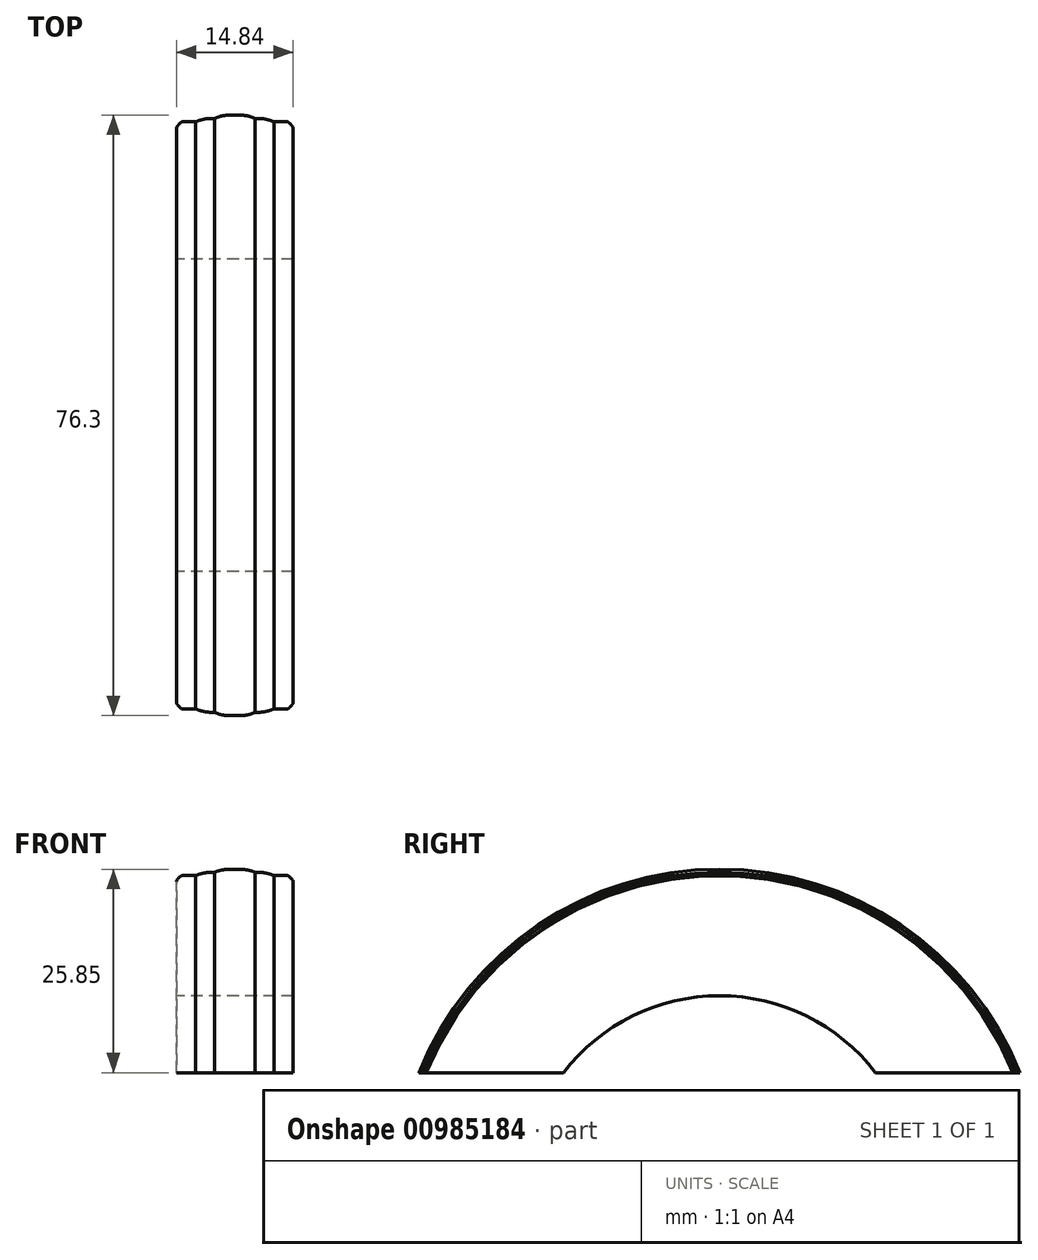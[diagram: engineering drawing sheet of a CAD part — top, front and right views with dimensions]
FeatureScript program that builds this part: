
annotation { "Feature Type Name" : "Feature", "Feature Type Description" : "" }
export const myFeature = defineFeature(function(context is Context, id is Id, definition is map)
    precondition{}
    {
        {
            var Q0;
            Q0=qCreatedBy(makeId("Front.planeOp"),FACE);
            var sketch = newSketch(context, id + "F0", { "sketchPlane" : qUnion([Q0])});
            skLineSegment(sketch, "E0", {"start": v(-55.67, 0) * mm, "end": v(68.03, 0) * mm, "construction": true});
            skLineSegment(sketch, "E1", {"start": v(-7.42, 0) * mm, "end": v(-7.42, 40.28) * mm});
            skLineSegment(sketch, "E2", {"start": v(-7.42, 40.28) * mm, "end": v(-4.96, 40.28) * mm});
            skLineSegment(sketch, "E3", {"start": v(-4.96, 40.28) * mm, "end": v(-4.96, 40.68) * mm});
            skLineSegment(sketch, "E4", {"start": v(-4.96, 40.68) * mm, "end": v(-2.58, 40.68) * mm});
            skLineSegment(sketch, "E5", {"start": v(-2.58, 40.68) * mm, "end": v(-2.58, 41.08) * mm});
            skLineSegment(sketch, "E6", {"start": v(-2.58, 41.08) * mm, "end": v(2.58, 41.08) * mm});
            skLineSegment(sketch, "E7", {"start": v(2.58, 41.08) * mm, "end": v(2.58, 40.68) * mm});
            skLineSegment(sketch, "E8", {"start": v(2.58, 40.68) * mm, "end": v(4.96, 40.68) * mm});
            skLineSegment(sketch, "E9", {"start": v(4.96, 40.68) * mm, "end": v(4.96, 40.28) * mm});
            skLineSegment(sketch, "E10", {"start": v(4.96, 40.28) * mm, "end": v(7.42, 40.28) * mm});
            skLineSegment(sketch, "E11", {"start": v(7.42, 40.28) * mm, "end": v(7.42, 0) * mm});
            skLineSegment(sketch, "E12", {"start": v(7.42, 0) * mm, "end": v(-7.42, 0) * mm});
            skLineSegment(sketch, "E13", {"start": v(0, 0) * mm, "end": v(0, 47.43) * mm, "construction": true});
            skSolve(sketch);
        }
        {
            var Q0;
            Q0=makeQuery(id+"F0.imprint","IMPRINT",FACE,{"disambiguationData":[TD([[makeQuery(id+"F0.imprint","IMPRINT",EDGE,{"derivedFrom":sQuery(id+"F0.wireOp",EDGE,"E1")}),-1.0]])]});
            var Q1;
            Q1=sQuery(id+"F0.wireOp",EDGE,"E0");
            revolve(context, id + "F1", {"surfaceOperationType" : NewSurfaceOperationType.NEW, "entities" : qUnion([Q0]), "axis" : qUnion([Q1]), "revolveType" : RevolveType.FULL});
        }
        {
            var Q0;
            Q0=makeQuery(id+"F1.opRevolve","SWEPT_EDGE",EDGE,{"disambiguationData":[OSD([sQuery(id+"F0.wireOp",EDGE,"E10"),sQuery(id+"F0.wireOp",EDGE,"E11")])]});
            var Q1;
            Q1=makeQuery(id+"F1.opRevolve","SWEPT_EDGE",EDGE,{"disambiguationData":[OSD([sQuery(id+"F0.wireOp",EDGE,"E1"),sQuery(id+"F0.wireOp",EDGE,"E2")])]});
            fillet(context, id + "F2", {"entities" : qUnion([Q0, Q1]), "radius" : 0.76 * mm, "tangentPropagation" : true, "rho" : 0.2, "crossSection" : FilletCrossSection.CONIC, "allowEdgeOverflow" : false});
        }
        {
            var Q0;
            Q0=makeQuery(id+"F1.opRevolve","SWEPT_EDGE",EDGE,{"disambiguationData":[OSD([sQuery(id+"F0.wireOp",EDGE,"E8"),sQuery(id+"F0.wireOp",EDGE,"E9")])]});
            var Q1;
            Q1=makeQuery(id+"F1.opRevolve","SWEPT_EDGE",EDGE,{"disambiguationData":[OSD([sQuery(id+"F0.wireOp",EDGE,"E3"),sQuery(id+"F0.wireOp",EDGE,"E4")])]});
            fillet(context, id + "F3", {"entities" : qUnion([Q0, Q1]), "radius" : 5.08 * mm, "tangentPropagation" : true, "allowEdgeOverflow" : false});
        }
        {
            var Q0;
            Q0=makeQuery(id+"F1.opRevolve","SWEPT_EDGE",EDGE,{"disambiguationData":[OSD([sQuery(id+"F0.wireOp",EDGE,"E6"),sQuery(id+"F0.wireOp",EDGE,"E7")])]});
            var Q1;
            Q1=makeQuery(id+"F1.opRevolve","SWEPT_EDGE",EDGE,{"disambiguationData":[OSD([sQuery(id+"F0.wireOp",EDGE,"E5"),sQuery(id+"F0.wireOp",EDGE,"E6")])]});
            fillet(context, id + "F4", {"entities" : qUnion([Q0, Q1]), "radius" : 5.08 * mm, "tangentPropagation" : true, "allowEdgeOverflow" : false});
        }
        {
            var Q0;
            Q0=qCreatedBy(makeId("Right.planeOp"),FACE);
            var sketch = newSketch(context, id + "F5", { "sketchPlane" : qUnion([Q0])});
            skCircle(sketch, "E14", {"center": v(0, 0) * mm, "radius": 25 * mm});
            skSolve(sketch);
        }
        {
            var Q0;
            Q0=qSketchRegion(id+"F5",true);
            extrude(context, id + "F6", {"entities" : qUnion([Q0]), "operationType" : NewBodyOperationType.REMOVE, "endBound" : BoundingType.THROUGH_ALL, "depth" : 25.4 * mm, "offsetDistance" : 25.4 * mm, "hasSecondDirection" : true, "secondDirectionBound" : SecondDirectionBoundingType.THROUGH_ALL, "secondDirectionOppositeDirection" : true, "secondDirectionDepth" : 25.4 * mm});
        }
        {
            var Q0;
            Q0=qCreatedBy(makeId("Right.planeOp"),FACE);
            var sketch = newSketch(context, id + "F7", { "sketchPlane" : qUnion([Q0])});
            skLineSegment(sketch, "E15", {"start": v(0, 15.23) * mm, "end": v(-38.1, 15.23) * mm, "construction": true});
            skLineSegment(sketch, "E16.MirrorCS", {"start": v(0, 15.23) * mm, "end": v(38.1, 15.23) * mm, "construction": true});
            skLineSegment(sketch, "E17", {"start": v(-59.25, 15.23) * mm, "end": v(65.7, 15.23) * mm});
            skLineSegment(sketch, "E18", {"start": v(65.7, 15.23) * mm, "end": v(65.7, -43.9) * mm});
            skLineSegment(sketch, "E19", {"start": v(65.7, -43.9) * mm, "end": v(-59.25, -43.9) * mm});
            skLineSegment(sketch, "E20", {"start": v(-59.25, -43.9) * mm, "end": v(-59.25, 15.23) * mm});
            skSolve(sketch);
        }
        {
            var Q0;
            Q0=qSketchRegion(id+"F7",true);
            extrude(context, id + "F8", {"entities" : qUnion([Q0]), "operationType" : NewBodyOperationType.REMOVE, "endBound" : BoundingType.THROUGH_ALL, "oppositeDirection" : true, "depth" : 25.4 * mm, "offsetDistance" : 25.4 * mm, "hasSecondDirection" : true, "secondDirectionBound" : SecondDirectionBoundingType.THROUGH_ALL, "secondDirectionOppositeDirection" : false, "secondDirectionDepth" : 25.4 * mm});
        }
    });
